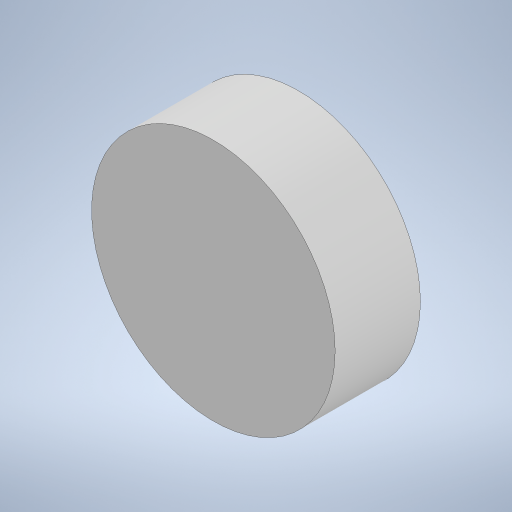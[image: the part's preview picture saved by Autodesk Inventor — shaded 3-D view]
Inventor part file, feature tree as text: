
AUTODESK INVENTOR PART (.ipt)
format: ipt  version: 2023.5 (Build 275446000, 446)  size: 199,168 bytes
history: native  units: mm
features: other x1, extrude x1, sketch x1
ambient origin geometry x8: Origin, YZ Plane, XZ Plane, XY Plane, X Axis, Y Axis, Z Axis, Center Point
bodies: Body1 (feature_tree)
feature tree (3):
  other  "Bryła1"
  extrude  "Wyciągnięcie proste1"  Depth=20.0mm
  sketch  "Szkic1"
